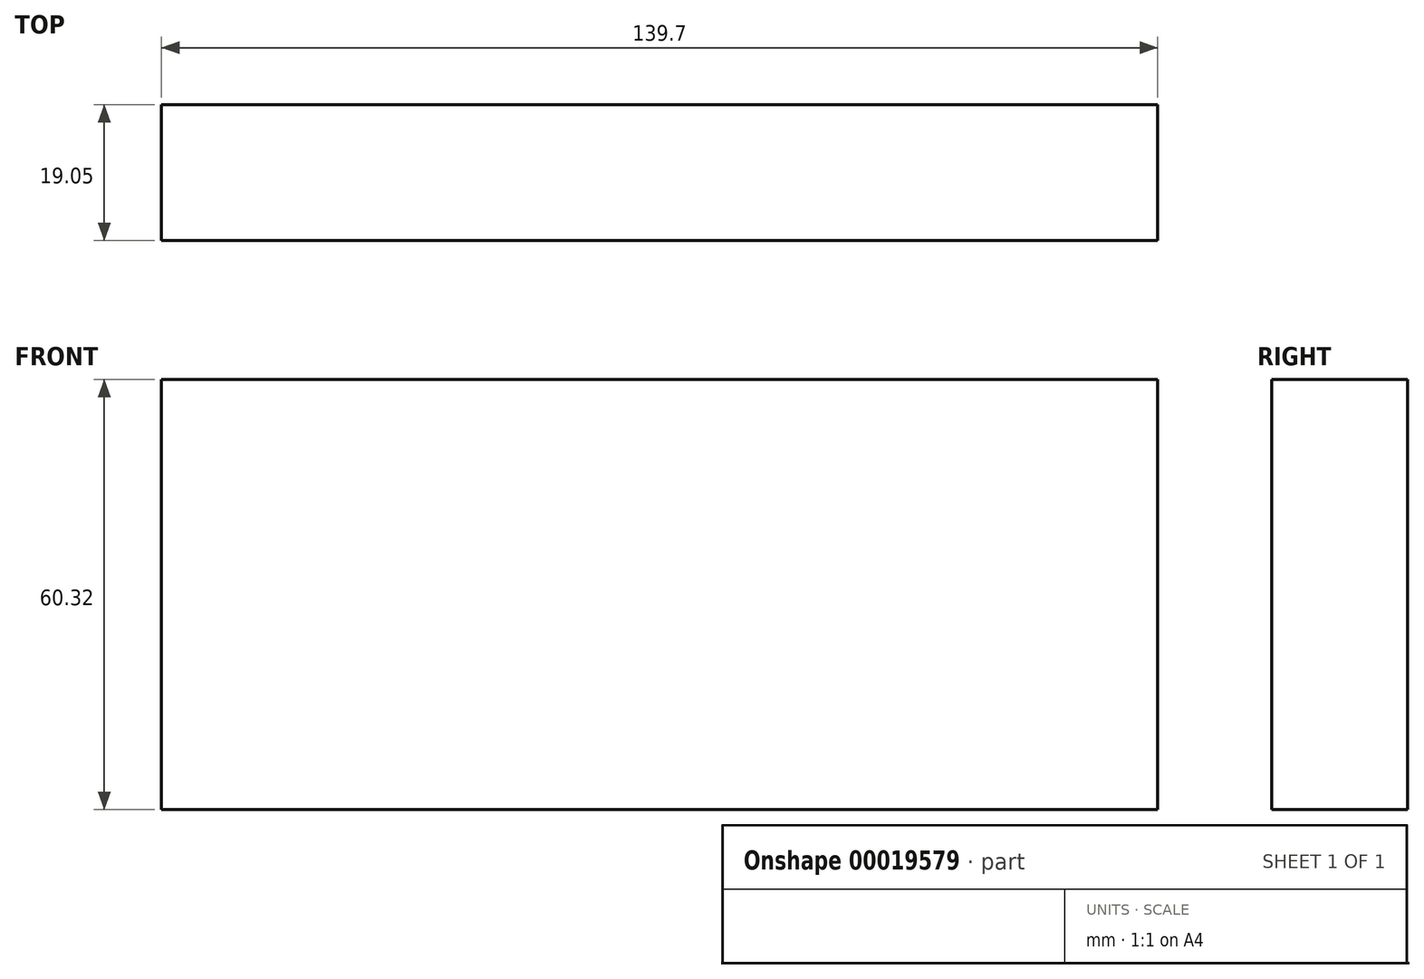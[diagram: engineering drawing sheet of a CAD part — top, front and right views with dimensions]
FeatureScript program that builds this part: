
annotation { "Feature Type Name" : "Feature", "Feature Type Description" : "" }
export const myFeature = defineFeature(function(context is Context, id is Id, definition is map)
    precondition{}
    {
        {
            var Q0;
            Q0=qCreatedBy(makeId("Front.planeOp"),FACE);
            var sketch = newSketch(context, id + "F0", { "sketchPlane" : qUnion([Q0])});
            skLineSegment(sketch, "E0.bottom", {"start": v(0, 0) * mm, "end": v(139.7, 0) * mm});
            skLineSegment(sketch, "E0.top", {"start": v(0, 60.32) * mm, "end": v(139.7, 60.32) * mm});
            skLineSegment(sketch, "E0.left", {"start": v(0, 0) * mm, "end": v(0, 60.32) * mm});
            skLineSegment(sketch, "E0.right", {"start": v(139.7, 0) * mm, "end": v(139.7, 60.32) * mm});
            skSolve(sketch);
        }
        {
            var Q0;
            Q0=makeQuery(id+"F0.imprint","IMPRINT",FACE,{"disambiguationData":[TD([[makeQuery(id+"F0.imprint","IMPRINT",EDGE,{"derivedFrom":sQuery(id+"F0.wireOp",EDGE,"E0.bottom")}),1.0]])]});
            extrude(context, id + "F1", {"entities" : qUnion([Q0]), "depth" : 19.05 * mm});
        }
    });
